# Revit family: Gira_216800
name_source: partatom
category: Elektroinstallationen
revit_build: Autodesk Revit 2017 (Build: 20160225_1515(x64)
units: mm (PartAtom-declared; Revit-internal decimal feet)

## family parameters
Basisbauteil = Fläche
Beim Laden mit Abzugskörper schneiden = Nein
Bemaßung runder Anschluss = Durchmesser verwenden
Beschriftungsausrichtung beibehalten = Nein
Gemeinsam genutzt = Nein
Raumberechnungspunkt = Nein
Teiletyp = Normal

## types (1)
- IP-Schnittst. KNX REG
    Anzahl der Eingänge = 0
    BIM = https://media.stage.bim.site X1 REG KNX.rfa
    BIMSITE_PRODUCT_ID = 0970236d5dbcfd86767d418a7bd093ba7f5cd1af
    Beschreibung = KNX IP-Schnittstelle  REG plus Merkmale:  Zur Ankopplung eines PCs an den KNX Bus um KNX Komponenten zu adressieren, programmieren oder diagnostizieren.  Hinweise :  Versorgung über externe DC 24 V.
    Breite in Teilungseinheiten = 0
    Bussystem Funkbus = Nein
    Bussystem KNX = Nein
    Bussystem KNX-Funk = Nein
    Bussystem LON = Nein
    Bussystem Powernet = Nein
    Datenblatt = https://media.stage.bim.site
    Datenblatt 1 = https://media.stage.bim.site
    Funktion Schalten = Nein
    GTIN = 4010337084457
    HAN = 216800
    HeinzeBIM = https://www.heinze.de
    Hersteller = Gira
    Kosten = 0 $
    Max. Anzahl der Jalousieausgänge = 0
    Max. Schaltleistung [Voltampere] = 0
    Mit Busankopplung = Nein
    Mit LED-Anzeige = Nein
    Produktseite = https://media.stage.bim.site
    Typname = IP-Schnittst. KNX REG
    URL = https://www.gira.de
    Vor Ort-/Handbedienung = Nein
    Vorgabe-Ansicht = 1219 mm

## geometry (parser evidence)
native form markers: Sweep x2
no freeform markers — native parametric forms only
